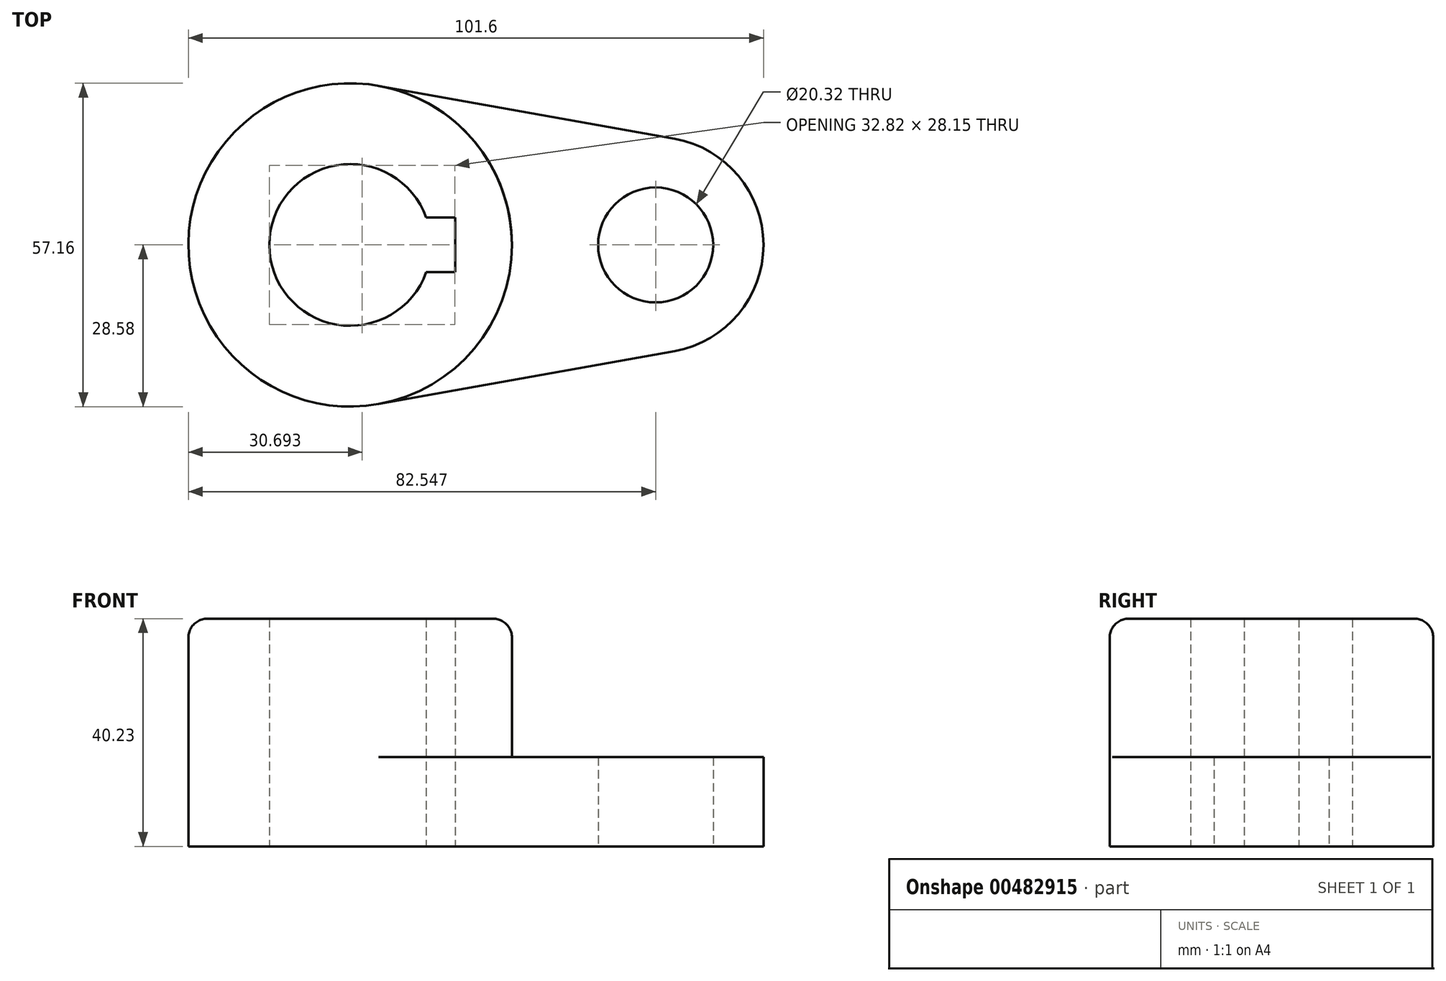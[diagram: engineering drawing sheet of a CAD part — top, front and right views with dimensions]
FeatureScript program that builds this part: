
annotation { "Feature Type Name" : "Feature", "Feature Type Description" : "" }
export const myFeature = defineFeature(function(context is Context, id is Id, definition is map)
    precondition{}
    {
        {
            var Q0;
            Q0=qCreatedBy(makeId("Top.planeOp"),FACE);
            var sketch = newSketch(context, id + "F0", { "sketchPlane" : qUnion([Q0])});
            skCircle(sketch, "E0", {"center": v(26.99, 0) * mm, "radius": 10.16 * mm});
            skArc(sketch, "E1", {"start": v(-21.94, 28.13) * mm, "mid": v(-55.56, 0) * mm, "end": v(-21.94, -28.13) * mm});
            skArc(sketch, "E2", {"start": v(30.35, -18.75) * mm, "mid": v(46.04, 0) * mm, "end": v(30.35, 18.75) * mm});
            skLineSegment(sketch, "E3", {"start": v(-21.94, 28.13) * mm, "end": v(30.35, 18.75) * mm});
            skLineSegment(sketch, "E4", {"start": v(-21.94, -28.13) * mm, "end": v(30.35, -18.75) * mm});
            skSolve(sketch);
        }
        {
            var Q0;
            Q0 = qSketchRegion(id + "F0", true);
            extrude(context, id + "F1", {"entities" : qUnion([Q0]), "depth" : 15.77 * mm});
        }
        {
            var Q0;
            Q0=makeQuery(id+"F1.opExtrude","CAP_FACE",FACE,{"disambiguationData":[OSD([sQuery(id+"F0.wireOp",EDGE,"E0"),sQuery(id+"F0.wireOp",EDGE,"E1"),sQuery(id+"F0.wireOp",EDGE,"E2"),sQuery(id+"F0.wireOp",EDGE,"E3"),sQuery(id+"F0.wireOp",EDGE,"E4")])],"isStart":false});
            var sketch = newSketch(context, id + "F2", { "sketchPlane" : qUnion([Q0])});
            skCircle(sketch, "E5", {"center": v(-26.99, 0) * mm, "radius": 28.58 * mm});
            skArc(sketch, "E6", {"start": v(-13.54, 4.83) * mm, "mid": v(-41.27, 0) * mm, "end": v(-13.54, -4.83) * mm});
            skPoint(sketch, "E7", {"position": v(26.99, 0) * mm});
            skLineSegment(sketch, "E8.bottom", {"start": v(-13.54, 4.83) * mm, "end": v(-8.46, 4.83) * mm});
            skLineSegment(sketch, "E8.top", {"start": v(-13.54, -4.83) * mm, "end": v(-8.46, -4.83) * mm});
            skLineSegment(sketch, "E8.right", {"start": v(-8.46, 4.83) * mm, "end": v(-8.46, -4.83) * mm});
            skSolve(sketch);
        }
        {
            var Q0;
            Q0=makeQuery(id+"F2.imprint","IMPRINT",FACE,{"disambiguationData":[TD([[makeQuery(id+"F2.imprint","IMPRINT",EDGE,{"derivedFrom":sQuery(id+"F2.wireOp",EDGE,"E6")}),-1.0]])]});
            extrude(context, id + "F3", {"entities" : qUnion([Q0]), "operationType" : NewBodyOperationType.ADD, "depth" : 24.46 * mm});
        }
        {
            var Q0;
            Q0=makeQuery(id+"F3.opExtrude","CAP_FACE",FACE,{"disambiguationData":[OSD([sQuery(id+"F2.wireOp",EDGE,"E5"),sQuery(id+"F2.wireOp",EDGE,"E6"),sQuery(id+"F2.wireOp",EDGE,"E8.bottom"),sQuery(id+"F2.wireOp",EDGE,"E8.top"),sQuery(id+"F2.wireOp",EDGE,"E8.right")])],"isStart":false});
            var sketch = newSketch(context, id + "F4", { "sketchPlane" : qUnion([Q0])});
            skArc(sketch, "E9.0", {"start": v(-13.54, 4.83) * mm, "mid": v(-41.27, 0) * mm, "end": v(-13.54, -4.83) * mm});
            skLineSegment(sketch, "E9.1", {"start": v(-8.46, 4.83) * mm, "end": v(-8.46, -4.83) * mm});
            skLineSegment(sketch, "E9.2", {"start": v(-13.54, -4.83) * mm, "end": v(-8.46, -4.83) * mm});
            skLineSegment(sketch, "E9.3", {"start": v(-13.54, 4.83) * mm, "end": v(-8.46, 4.83) * mm});
            skSolve(sketch);
        }
        {
            var Q0;
            Q0 = qSketchRegion(id + "F4", true);
            extrude(context, id + "F5", {"entities" : qUnion([Q0]), "operationType" : NewBodyOperationType.REMOVE, "endBound" : BoundingType.THROUGH_ALL, "oppositeDirection" : true, "depth" : 25.4 * mm});
        }
        {
            var Q0;
            Q0=makeQuery(id+"F3.opExtrude","CAP_EDGE",EDGE,{"disambiguationData":[OSD([sQuery(id+"F2.wireOp",EDGE,"E5")])],"isStart":false});
            fillet(context, id + "F6", {"entities" : qUnion([Q0]), "radius" : 3.3 * mm, "tangentPropagation" : true, "allowEdgeOverflow" : false});
        }
    });
